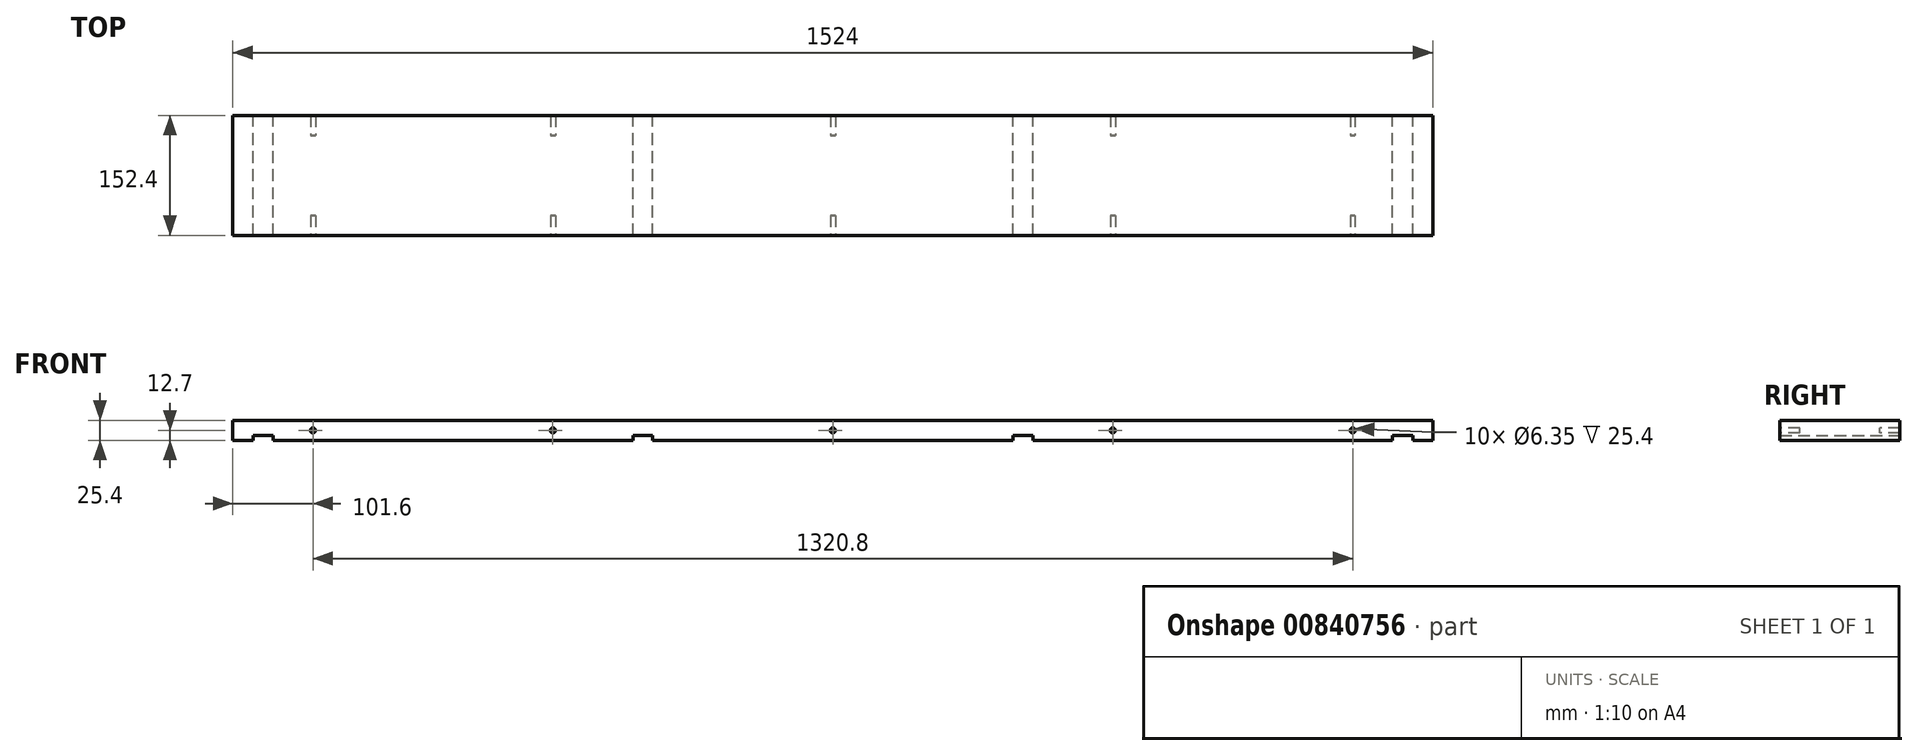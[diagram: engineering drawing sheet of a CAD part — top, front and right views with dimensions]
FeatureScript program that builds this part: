
annotation { "Feature Type Name" : "Feature", "Feature Type Description" : "" }
export const myFeature = defineFeature(function(context is Context, id is Id, definition is map)
    precondition{}
    {
        {
            var Q0;
            Q0=qCreatedBy(makeId("Top.planeOp"),FACE);
            var sketch = newSketch(context, id + "F0", { "sketchPlane" : qUnion([Q0])});
            skLineSegment(sketch, "E0.bottom", {"start": v(0, 0) * mm, "end": v(1524, 0) * mm});
            skLineSegment(sketch, "E0.top", {"start": v(0, 152.4) * mm, "end": v(1524, 152.4) * mm});
            skLineSegment(sketch, "E0.left", {"start": v(0, 0) * mm, "end": v(0, 152.4) * mm});
            skLineSegment(sketch, "E0.right", {"start": v(1524, 0) * mm, "end": v(1524, 152.4) * mm});
            skSolve(sketch);
        }
        {
            var Q0;
            Q0=makeQuery(id+"F0.imprint","IMPRINT",FACE,{"disambiguationData":[TD([[makeQuery(id+"F0.imprint","IMPRINT",EDGE,{"derivedFrom":sQuery(id+"F0.wireOp",EDGE,"E0.bottom")}),1.0]])]});
            extrude(context, id + "F1", {"entities" : qUnion([Q0]), "depth" : 25.4 * mm, "offsetDistance" : 25.4 * mm});
        }
        {
            var Q0;
            Q0=qCreatedBy(makeId("Top.planeOp"),FACE);
            var sketch = newSketch(context, id + "F2", { "sketchPlane" : qUnion([Q0])});
            skLineSegment(sketch, "E1.bottom", {"start": v(25.4, -30.93) * mm, "end": v(50.8, -30.93) * mm});
            skLineSegment(sketch, "E1.top", {"start": v(25.4, 184.97) * mm, "end": v(50.8, 184.97) * mm});
            skLineSegment(sketch, "E1.left", {"start": v(25.4, -30.93) * mm, "end": v(25.4, 184.97) * mm});
            skLineSegment(sketch, "E1.right", {"start": v(50.8, -30.93) * mm, "end": v(50.8, 184.97) * mm});
            skLineSegment(sketch, "E2.bottom", {"start": v(508, -30.93) * mm, "end": v(533.4, -30.93) * mm});
            skLineSegment(sketch, "E2.top", {"start": v(508, 184.97) * mm, "end": v(533.4, 184.97) * mm});
            skLineSegment(sketch, "E2.left", {"start": v(508, -30.93) * mm, "end": v(508, 184.97) * mm});
            skLineSegment(sketch, "E2.right", {"start": v(533.4, -30.93) * mm, "end": v(533.4, 184.97) * mm});
            skLineSegment(sketch, "E3.bottom", {"start": v(990.6, -30.93) * mm, "end": v(1016, -30.93) * mm});
            skLineSegment(sketch, "E3.top", {"start": v(990.6, 184.97) * mm, "end": v(1016, 184.97) * mm});
            skLineSegment(sketch, "E3.left", {"start": v(990.6, -30.93) * mm, "end": v(990.6, 184.97) * mm});
            skLineSegment(sketch, "E3.right", {"start": v(1016, -30.93) * mm, "end": v(1016, 184.97) * mm});
            skLineSegment(sketch, "E4.bottom", {"start": v(1473.2, -30.93) * mm, "end": v(1498.6, -30.93) * mm});
            skLineSegment(sketch, "E4.top", {"start": v(1473.2, 184.97) * mm, "end": v(1498.6, 184.97) * mm});
            skLineSegment(sketch, "E4.left", {"start": v(1473.2, -30.93) * mm, "end": v(1473.2, 184.97) * mm});
            skLineSegment(sketch, "E4.right", {"start": v(1498.6, -30.93) * mm, "end": v(1498.6, 184.97) * mm});
            skSolve(sketch);
        }
        {
            var Q0;
            Q0=makeQuery(id+"F2.imprint","IMPRINT",FACE,{"disambiguationData":[TD([[makeQuery(id+"F2.imprint","IMPRINT",EDGE,{"derivedFrom":sQuery(id+"F2.wireOp",EDGE,"E1.bottom")}),1.0]])]});
            var Q1;
            Q1=makeQuery(id+"F2.imprint","IMPRINT",FACE,{"disambiguationData":[TD([[makeQuery(id+"F2.imprint","IMPRINT",EDGE,{"derivedFrom":sQuery(id+"F2.wireOp",EDGE,"E2.bottom")}),1.0]])]});
            var Q2;
            Q2=makeQuery(id+"F2.imprint","IMPRINT",FACE,{"disambiguationData":[TD([[makeQuery(id+"F2.imprint","IMPRINT",EDGE,{"derivedFrom":sQuery(id+"F2.wireOp",EDGE,"E3.bottom")}),1.0]])]});
            var Q3;
            Q3=makeQuery(id+"F2.imprint","IMPRINT",FACE,{"disambiguationData":[TD([[makeQuery(id+"F2.imprint","IMPRINT",EDGE,{"derivedFrom":sQuery(id+"F2.wireOp",EDGE,"E4.bottom")}),1.0]])]});
            extrude(context, id + "F3", {"entities" : qUnion([Q0, Q1, Q2, Q3]), "operationType" : NewBodyOperationType.REMOVE, "depth" : 6.35 * mm, "offsetDistance" : 25.4 * mm});
        }
        {
            var Q0;
            Q0=qCreatedBy(makeId("Front.planeOp"),FACE);
            var sketch = newSketch(context, id + "F4", { "sketchPlane" : qUnion([Q0])});
            skCircle(sketch, "E5", {"center": v(101.6, 12.7) * mm, "radius": 3.18 * mm});
            skCircle(sketch, "E6", {"center": v(406.4, 12.7) * mm, "radius": 3.18 * mm});
            skCircle(sketch, "E7", {"center": v(762, 12.7) * mm, "radius": 3.18 * mm});
            skCircle(sketch, "E8", {"center": v(1117.6, 12.7) * mm, "radius": 3.18 * mm});
            skCircle(sketch, "E9", {"center": v(1422.4, 12.7) * mm, "radius": 3.18 * mm});
            skSolve(sketch);
        }
        {
            var Q0;
            Q0=makeQuery(id+"F4.imprint","IMPRINT",FACE,{"disambiguationData":[TD([[makeQuery(id+"F4.imprint","IMPRINT",EDGE,{"derivedFrom":sQuery(id+"F4.wireOp",EDGE,"E5")}),1.0]])]});
            var Q1;
            Q1=makeQuery(id+"F4.imprint","IMPRINT",FACE,{"disambiguationData":[TD([[makeQuery(id+"F4.imprint","IMPRINT",EDGE,{"derivedFrom":sQuery(id+"F4.wireOp",EDGE,"E6")}),1.0]])]});
            var Q2;
            Q2=makeQuery(id+"F4.imprint","IMPRINT",FACE,{"disambiguationData":[TD([[makeQuery(id+"F4.imprint","IMPRINT",EDGE,{"derivedFrom":sQuery(id+"F4.wireOp",EDGE,"E7")}),1.0]])]});
            var Q3;
            Q3=makeQuery(id+"F4.imprint","IMPRINT",FACE,{"disambiguationData":[TD([[makeQuery(id+"F4.imprint","IMPRINT",EDGE,{"derivedFrom":sQuery(id+"F4.wireOp",EDGE,"E8")}),1.0]])]});
            var Q4;
            Q4=makeQuery(id+"F4.imprint","IMPRINT",FACE,{"disambiguationData":[TD([[makeQuery(id+"F4.imprint","IMPRINT",EDGE,{"derivedFrom":sQuery(id+"F4.wireOp",EDGE,"E9")}),1.0]])]});
            extrude(context, id + "F5", {"entities" : qUnion([Q0, Q1, Q2, Q3, Q4]), "operationType" : NewBodyOperationType.REMOVE, "oppositeDirection" : true, "depth" : 25.4 * mm, "offsetDistance" : 25.4 * mm});
        }
        {
            var Q0;
            Q0=makeQuery(id+"F4.imprint","IMPRINT",FACE,{"disambiguationData":[TD([[makeQuery(id+"F4.imprint","IMPRINT",EDGE,{"derivedFrom":sQuery(id+"F4.wireOp",EDGE,"E7")}),1.0]])]});
            var Q1;
            Q1=makeQuery(id+"F4.imprint","IMPRINT",FACE,{"disambiguationData":[TD([[makeQuery(id+"F4.imprint","IMPRINT",EDGE,{"derivedFrom":sQuery(id+"F4.wireOp",EDGE,"E8")}),1.0]])]});
            var Q2;
            Q2=makeQuery(id+"F4.imprint","IMPRINT",FACE,{"disambiguationData":[TD([[makeQuery(id+"F4.imprint","IMPRINT",EDGE,{"derivedFrom":sQuery(id+"F4.wireOp",EDGE,"E9")}),1.0]])]});
            var Q3;
            Q3=makeQuery(id+"F4.imprint","IMPRINT",FACE,{"disambiguationData":[TD([[makeQuery(id+"F4.imprint","IMPRINT",EDGE,{"derivedFrom":sQuery(id+"F4.wireOp",EDGE,"E6")}),1.0]])]});
            var Q4;
            Q4=makeQuery(id+"F4.imprint","IMPRINT",FACE,{"disambiguationData":[TD([[makeQuery(id+"F4.imprint","IMPRINT",EDGE,{"derivedFrom":sQuery(id+"F4.wireOp",EDGE,"E5")}),1.0]])]});
            extrude(context, id + "F6", {"entities" : qUnion([Q0, Q1, Q2, Q3, Q4]), "operationType" : NewBodyOperationType.REMOVE, "oppositeDirection" : true, "depth" : 152.4 * mm, "offsetDistance" : 25.4 * mm, "hasSecondDirection" : true, "secondDirectionOppositeDirection" : true, "secondDirectionDepth" : 127 * mm});
        }
    });
